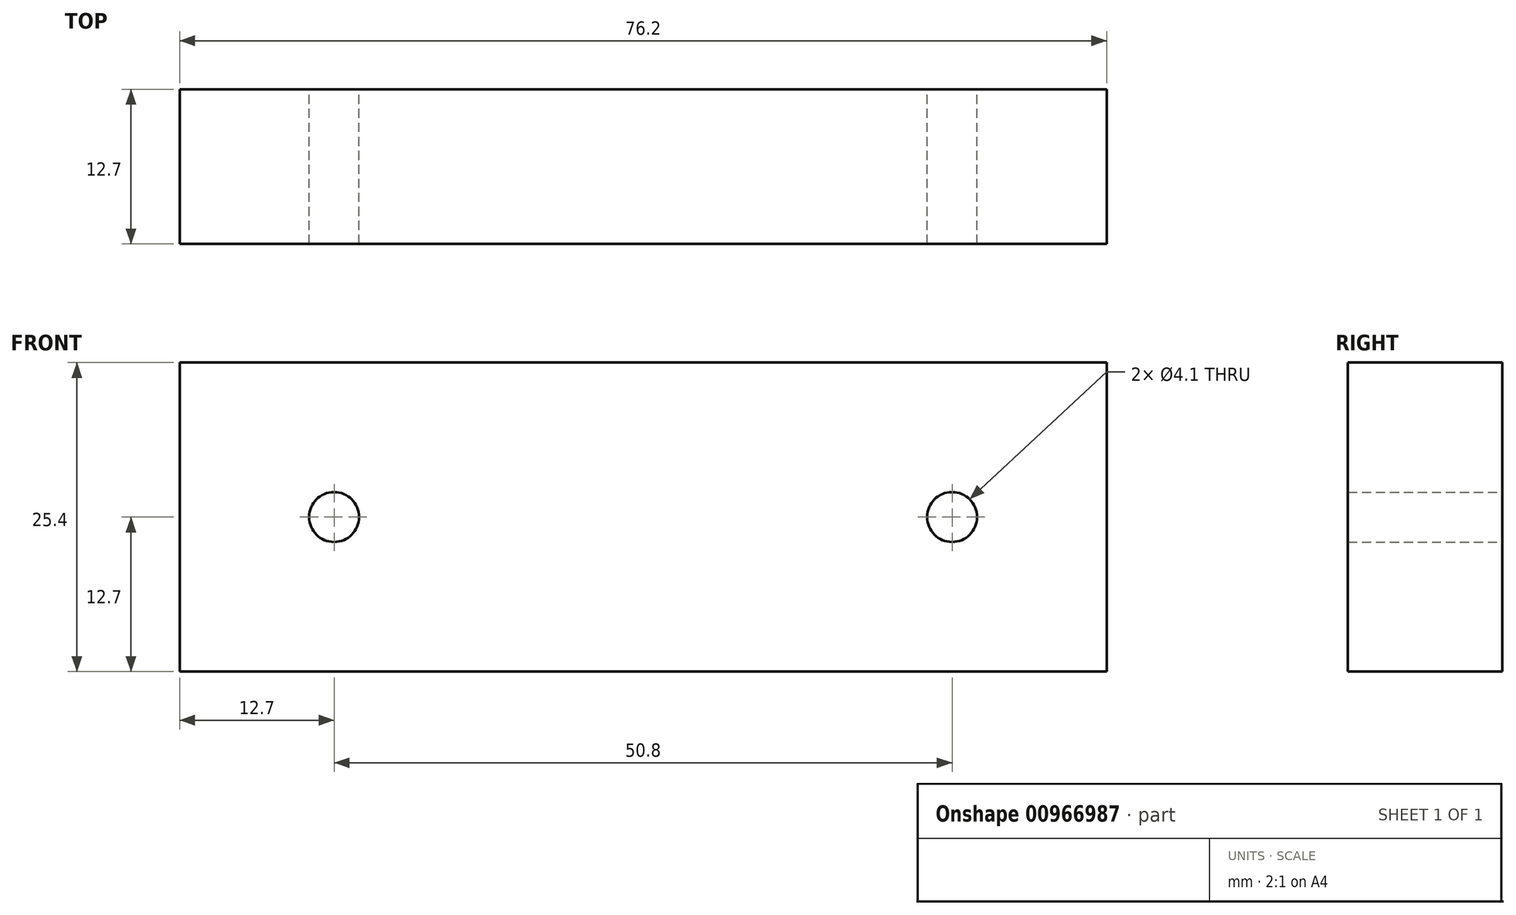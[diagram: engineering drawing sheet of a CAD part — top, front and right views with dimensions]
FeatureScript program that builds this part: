
annotation { "Feature Type Name" : "Feature", "Feature Type Description" : "" }
export const myFeature = defineFeature(function(context is Context, id is Id, definition is map)
    precondition{}
    {
        {
            var Q0;
            Q0=qCreatedBy(makeId("Front.planeOp"),FACE);
            var sketch = newSketch(context, id + "F0", { "sketchPlane" : qUnion([Q0])});
            skLineSegment(sketch, "E0.bottom", {"start": v(0, 0) * mm, "end": v(76.2, 0) * mm});
            skLineSegment(sketch, "E0.top", {"start": v(0, 25.4) * mm, "end": v(76.2, 25.4) * mm});
            skLineSegment(sketch, "E0.left", {"start": v(0, 0) * mm, "end": v(0, 25.4) * mm});
            skLineSegment(sketch, "E0.right", {"start": v(76.2, 0) * mm, "end": v(76.2, 25.4) * mm});
            skLineSegment(sketch, "E1", {"start": v(76.2, 12.7) * mm, "end": v(0, 12.7) * mm, "construction": true});
            skLineSegment(sketch, "E2", {"start": v(38.1, 25.4) * mm, "end": v(38.1, 0) * mm, "construction": true});
            skCircle(sketch, "E3", {"center": v(12.7, 12.7) * mm, "radius": 2.05 * mm});
            skCircle(sketch, "E4", {"center": v(63.5, 12.7) * mm, "radius": 2.05 * mm});
            skSolve(sketch);
        }
        {
            var Q0;
            Q0 = qSketchRegion(id + "F0", true);
            extrude(context, id + "F1", {"entities" : qUnion([Q0]), "depth" : 12.7 * mm, "offsetDistance" : 25 * mm});
        }
    });
